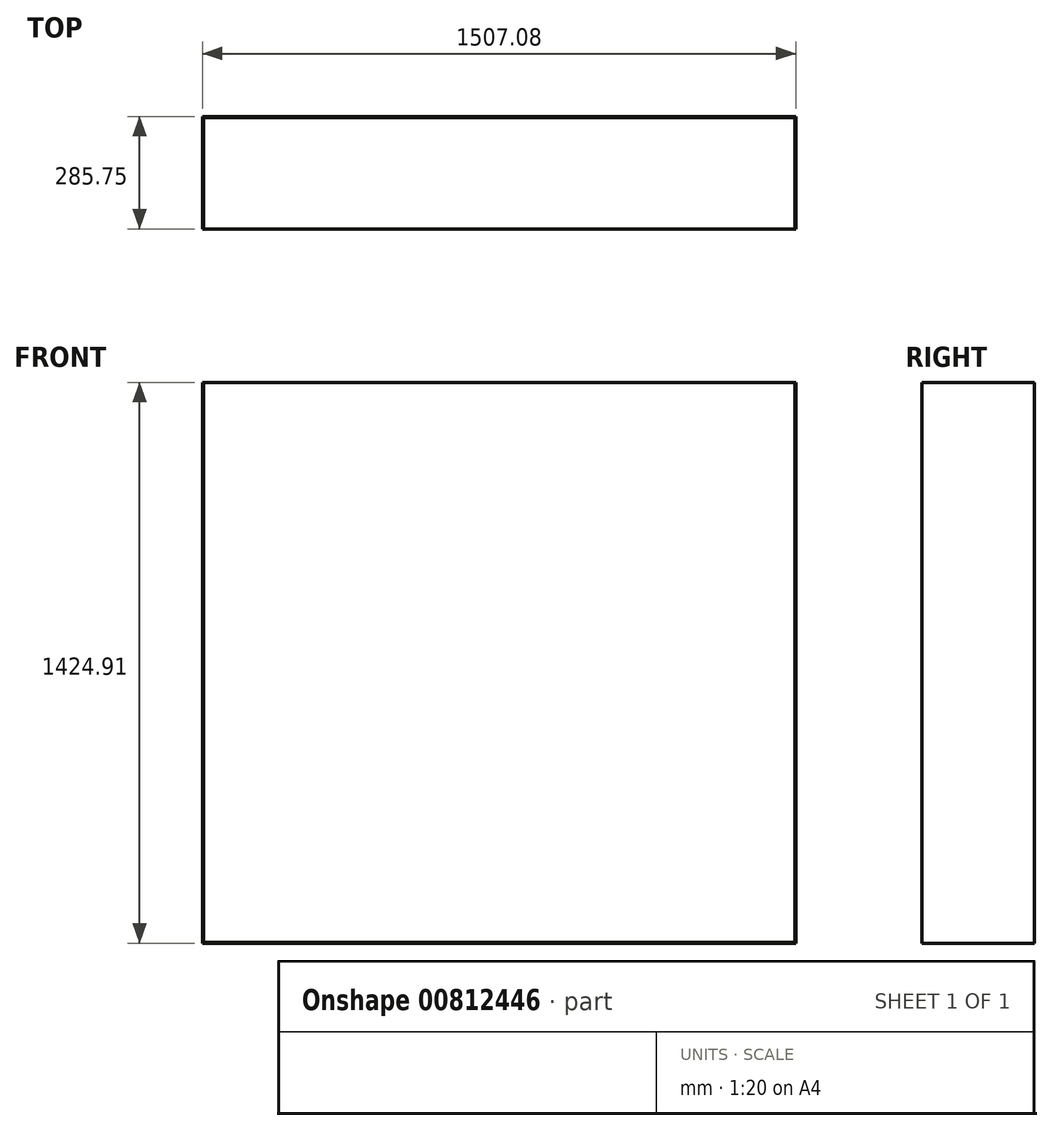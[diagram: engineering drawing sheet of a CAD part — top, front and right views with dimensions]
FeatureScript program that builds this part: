
annotation { "Feature Type Name" : "Feature", "Feature Type Description" : "" }
export const myFeature = defineFeature(function(context is Context, id is Id, definition is map)
    precondition{}
    {
        {
            var Q0;
            Q0=qCreatedBy(makeId("Front.planeOp"),FACE);
            var sketch = newSketch(context, id + "F0", { "sketchPlane" : qUnion([Q0])});
            skLineSegment(sketch, "E0.bottom", {"start": v(-442.7, 1343.1) * mm, "end": v(1064.37, 1343.1) * mm});
            skLineSegment(sketch, "E0.top", {"start": v(-442.7, -81.8) * mm, "end": v(1064.37, -81.8) * mm});
            skLineSegment(sketch, "E0.left", {"start": v(-442.7, 1343.1) * mm, "end": v(-442.7, -81.8) * mm});
            skLineSegment(sketch, "E0.right", {"start": v(1064.37, 1343.1) * mm, "end": v(1064.37, -81.8) * mm});
            skSolve(sketch);
        }
        {
            var Q0;
            Q0=makeQuery(id+"F0.imprint","IMPRINT",FACE,{"disambiguationData":[TD([[makeQuery(id+"F0.imprint","IMPRINT",EDGE,{"derivedFrom":sQuery(id+"F0.wireOp",EDGE,"E0.bottom")}),-1.0]])]});
            extrude(context, id + "F1", {"entities" : qUnion([Q0]), "depth" : 285.75 * mm, "offsetDistance" : 25.4 * mm});
        }
        {
            var Q0;
            Q0=makeQuery(id+"F1.opExtrude","CAP_FACE",FACE,{"disambiguationData":[OSD([sQuery(id+"F0.wireOp",EDGE,"E0.bottom"),sQuery(id+"F0.wireOp",EDGE,"E0.top"),sQuery(id+"F0.wireOp",EDGE,"E0.left"),sQuery(id+"F0.wireOp",EDGE,"E0.right")])],"isStart":false});
            var Q1;
            Q1=makeQuery(id+"F1.opExtrude","SWEPT_FACE",FACE,{"disambiguationData":[OSD([sQuery(id+"F0.wireOp",EDGE,"E0.bottom")])]});
            shell(context, id + "F2", {"entities" : qUnion([Q0, Q1]), "thickness" : 2.54 * mm});
        }
    });
